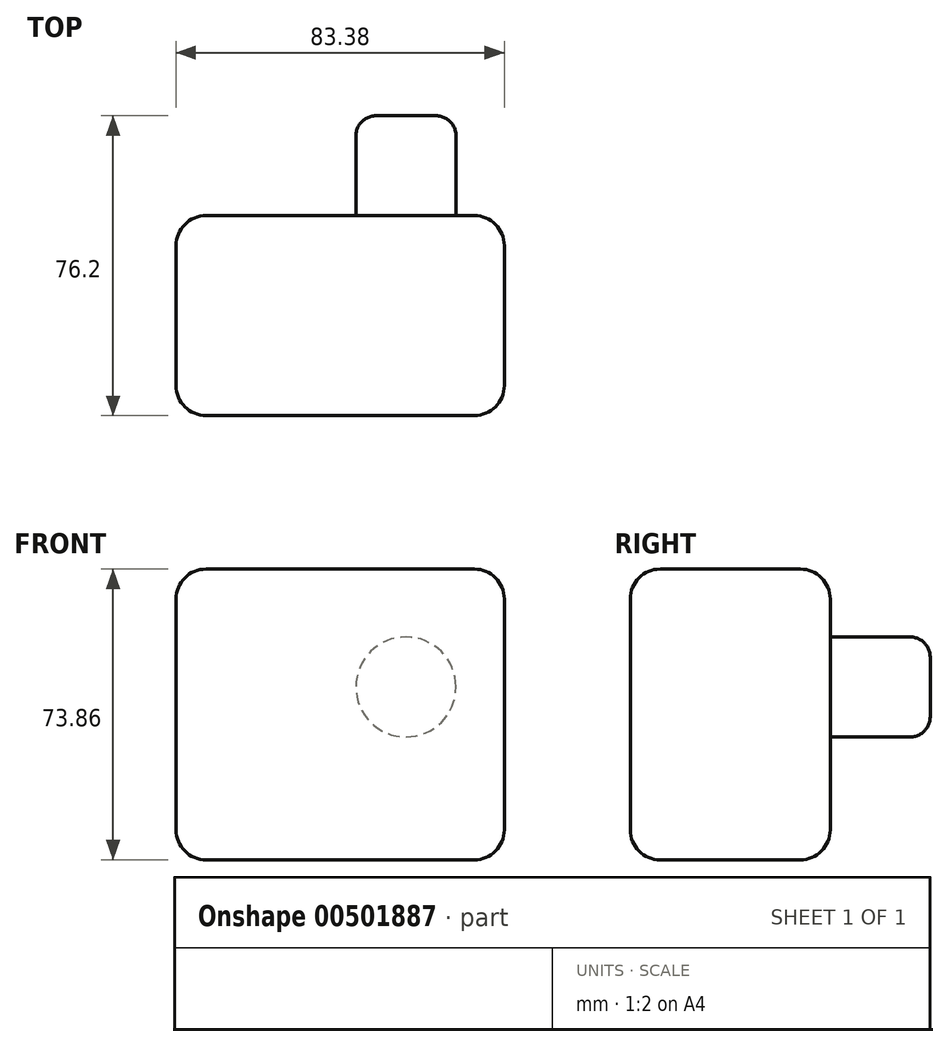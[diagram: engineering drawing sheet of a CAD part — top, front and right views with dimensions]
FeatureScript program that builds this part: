
annotation { "Feature Type Name" : "Feature", "Feature Type Description" : "" }
export const myFeature = defineFeature(function(context is Context, id is Id, definition is map)
    precondition{}
    {
        {
            var Q0;
            Q0=qCreatedBy(makeId("Front.planeOp"),FACE);
            var sketch = newSketch(context, id + "F0", { "sketchPlane" : qUnion([Q0])});
            skLineSegment(sketch, "E0", {"start": v(-50.07, 61.41) * mm, "end": v(-50.07, -12.45) * mm});
            skLineSegment(sketch, "E1", {"start": v(-50.07, -12.45) * mm, "end": v(33.31, -12.45) * mm});
            skLineSegment(sketch, "E2", {"start": v(33.31, -12.45) * mm, "end": v(33.31, 61.41) * mm});
            skLineSegment(sketch, "E3", {"start": v(33.31, 61.41) * mm, "end": v(-50.07, 61.41) * mm});
            skSolve(sketch);
        }
        {
            var Q0;
            Q0=makeQuery(id+"F0.imprint","IMPRINT",FACE,{"disambiguationData":[TD([[makeQuery(id+"F0.imprint","IMPRINT",EDGE,{"derivedFrom":sQuery(id+"F0.wireOp",EDGE,"E0")}),1.0]])]});
            extrude(context, id + "F1", {"entities" : qUnion([Q0]), "endBound" : BoundingType.SYMMETRIC, "oppositeDirection" : true, "depth" : 50.8 * mm});
        }
        {
            var Q0;
            Q0=makeQuery(id+"F1.opExtrude","SWEPT_EDGE",EDGE,{"disambiguationData":[OSD([sQuery(id+"F0.wireOp",EDGE,"E0"),sQuery(id+"F0.wireOp",EDGE,"E1")])]});
            var Q1;
            Q1=makeQuery(id+"F1.opExtrude","SWEPT_EDGE",EDGE,{"disambiguationData":[OSD([sQuery(id+"F0.wireOp",EDGE,"E1"),sQuery(id+"F0.wireOp",EDGE,"E2")])]});
            var Q2;
            Q2=makeQuery(id+"F1.opExtrude","SWEPT_EDGE",EDGE,{"disambiguationData":[OSD([sQuery(id+"F0.wireOp",EDGE,"E2"),sQuery(id+"F0.wireOp",EDGE,"E3")])]});
            var Q3;
            Q3=makeQuery(id+"F1.opExtrude","SWEPT_EDGE",EDGE,{"disambiguationData":[OSD([sQuery(id+"F0.wireOp",EDGE,"E0"),sQuery(id+"F0.wireOp",EDGE,"E3")])]});
            var Q4;
            Q4=makeQuery(id+"F1.opExtrude","SWEPT_FACE",FACE,{"disambiguationData":[OSD([sQuery(id+"F0.wireOp",EDGE,"E0")])]});
            var Q5;
            Q5=makeQuery(id+"F1.opExtrude","CAP_FACE",FACE,{"disambiguationData":[OSD([sQuery(id+"F0.wireOp",EDGE,"E0"),sQuery(id+"F0.wireOp",EDGE,"E1"),sQuery(id+"F0.wireOp",EDGE,"E2"),sQuery(id+"F0.wireOp",EDGE,"E3")])],"isStart":true});
            var Q6;
            Q6=makeQuery(id+"F1.opExtrude","SWEPT_FACE",FACE,{"disambiguationData":[OSD([sQuery(id+"F0.wireOp",EDGE,"E3")])]});
            var Q7;
            Q7=makeQuery(id+"F1.opExtrude","SWEPT_FACE",FACE,{"disambiguationData":[OSD([sQuery(id+"F0.wireOp",EDGE,"E1")])]});
            var Q8;
            Q8=makeQuery(id+"F1.opExtrude","CAP_FACE",FACE,{"disambiguationData":[OSD([sQuery(id+"F0.wireOp",EDGE,"E0"),sQuery(id+"F0.wireOp",EDGE,"E1"),sQuery(id+"F0.wireOp",EDGE,"E2"),sQuery(id+"F0.wireOp",EDGE,"E3")])],"isStart":false});
            var Q9;
            Q9=makeQuery(id+"F1.opExtrude","SWEPT_FACE",FACE,{"disambiguationData":[OSD([sQuery(id+"F0.wireOp",EDGE,"E2")])]});
            fillet(context, id + "F2", {"entities" : qUnion([Q0, Q1, Q2, Q3, Q4, Q5, Q6, Q7, Q8, Q9]), "radius" : 7.62 * mm, "tangentPropagation" : true, "allowEdgeOverflow" : false});
        }
        {
            var Q0;
            Q0=makeQuery(id+"F1.opExtrude","CAP_FACE",FACE,{"disambiguationData":[OSD([sQuery(id+"F0.wireOp",EDGE,"E0"),sQuery(id+"F0.wireOp",EDGE,"E1"),sQuery(id+"F0.wireOp",EDGE,"E2"),sQuery(id+"F0.wireOp",EDGE,"E3")])],"isStart":false});
            var sketch = newSketch(context, id + "F3", { "sketchPlane" : qUnion([Q0])});
            skCircle(sketch, "E4", {"center": v(-8.35, 31.47) * mm, "radius": 12.7 * mm});
            skSolve(sketch);
        }
        {
            var Q0;
            Q0=makeQuery(id+"F3.imprint","IMPRINT",FACE,{"disambiguationData":[TD([[makeQuery(id+"F3.imprint","IMPRINT",EDGE,{"derivedFrom":sQuery(id+"F3.wireOp",EDGE,"E4")}),1.0]])]});
            extrude(context, id + "F4", {"entities" : qUnion([Q0]), "operationType" : NewBodyOperationType.ADD, "depth" : 25.4 * mm});
        }
        {
            var Q0;
            Q0=makeQuery(id+"F4.opExtrude","CAP_EDGE",EDGE,{"disambiguationData":[OSD([sQuery(id+"F3.wireOp",EDGE,"E4")])],"isStart":false});
            fillet(context, id + "F5", {"entities" : qUnion([Q0]), "radius" : 5.08 * mm, "tangentPropagation" : true, "allowEdgeOverflow" : false});
        }
    });
